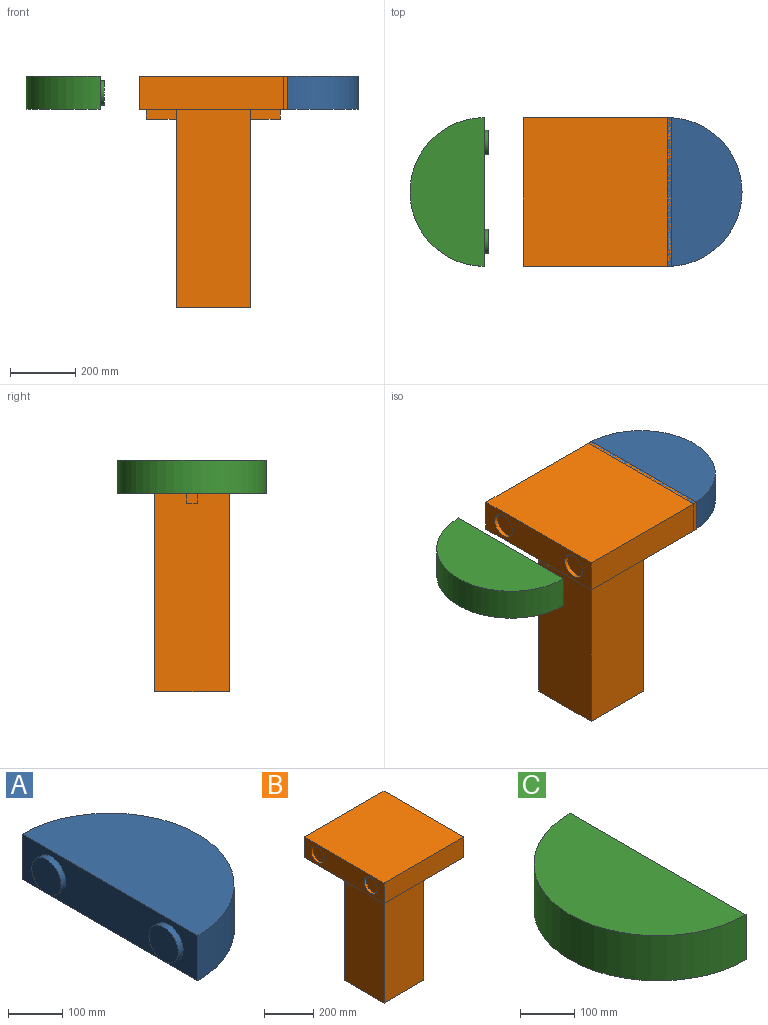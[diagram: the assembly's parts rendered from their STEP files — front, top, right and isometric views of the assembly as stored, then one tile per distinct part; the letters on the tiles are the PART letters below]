
ASSEMBLY  parts=3 mates=2
PART A: 8 faces, bbox 241.4x457.2x101.6 mm
  f0: plane 457.2x101.6mm, normal (-1,0,0), area 37330.8mm2, adj f1,f2,f3,f4,f6
  f1: cylinder r=228.6mm len=457.2mm, axis (0,0,-1), area 72965.9mm2, adj f0,f2,f3
  f2: plane 457.2x228.6mm, normal (0,0,1), area 82086.6mm2, adj f0,f1
  f3: plane 457.2x228.6mm, normal (0,0,-1), area 82086.6mm2, adj f0,f1
  f4: cylinder r=38.1mm len=76.2mm, axis (1,0,0), area 3064.6mm2, adj f0,f5
  f5: plane 76.2x76.2mm, normal (-1,0,0), area 4560.4mm2, adj f4
  f6: cylinder r=38.1mm len=76.2mm, axis (1,0,0), area 3064.6mm2, adj f0,f7
  f7: plane 76.2x76.2mm, normal (-1,0,0), area 4560.4mm2, adj f6
PART B: 27 faces, bbox 457.2x457.2x711.2 mm
  f0: plane 457.2x457.2mm, normal (0,0,-1), area 150642.3mm2, adj f1,f2,f3,f4,f14,f15,f16,f17
  f1: plane 457.2x101.6mm, normal (0,-1,0), area 46451.5mm2, adj f0,f2,f4,f5
  f2: plane 457.2x101.6mm, normal (1,0,0), area 37330.8mm2, adj f0,f1,f3,f5,f10,f12
  f3: plane 457.2x101.6mm, normal (0,1,0), area 46451.5mm2, adj f0,f2,f4,f5
  f4: plane 457.2x101.6mm, normal (-1,0,0), area 37330.8mm2, adj f0,f1,f3,f5,f6,f8
  f5: plane 457.2x457.2mm, normal (0,0,1), area 209031.8mm2, adj f1,f2,f3,f4
  f6: cylinder r=38.1mm len=76.2mm, axis (-1,0,0), area 3064.6mm2, adj f4,f7
  f7: plane 76.2x76.2mm, normal (-1,0,0), area 4560.4mm2, adj f6
  f8: cylinder r=38.1mm len=76.2mm, axis (-1,0,0), area 3064.6mm2, adj f4,f9
  f9: plane 76.2x76.2mm, normal (-1,0,0), area 4560.4mm2, adj f8
  f10: cylinder r=38.1mm len=76.2mm, axis (1,0,0), area 3064.6mm2, adj f2,f11
  f11: plane 76.2x76.2mm, normal (1,0,0), area 4560.4mm2, adj f10
  f12: cylinder r=38.1mm len=76.2mm, axis (1,0,0), area 3064.6mm2, adj f2,f13
  f13: plane 76.2x76.2mm, normal (1,0,0), area 4560.4mm2, adj f12
  f14: plane 609.6x228.6mm, normal (1,0,0), area 138332.6mm2, adj f0,f15,f17,f18,f23,f24,f25
  f15: plane 609.6x228.6mm, normal (0,-1,0), area 139354.6mm2, adj f0,f14,f16,f18
  f16: plane 609.6x228.6mm, normal (-1,0,0), area 138332.6mm2, adj f0,f15,f17,f18,f19,f21,f22
  f17: plane 609.6x228.6mm, normal (0,1,0), area 139354.6mm2, adj f0,f14,f16,f18
  f18: plane 228.6x228.6mm, normal (0,0,-1), area 52258mm2, adj f14,f15,f16,f17
  f19: plane 91.44x33.53mm, normal (0,0,-1), area 3065.8mm2, adj f16,f20,f21,f22
  f20: plane 33.53x30.48mm, normal (-1,0,0), area 1021.9mm2, adj f0,f19,f21,f22
  f21: plane 91.44x30.48mm, normal (0,1,0), area 2787.1mm2, adj f0,f16,f19,f20
  f22: plane 91.44x30.48mm, normal (0,-1,0), area 2787.1mm2, adj f0,f16,f19,f20
  f23: plane 91.44x33.53mm, normal (0,0,-1), area 3065.8mm2, adj f14,f24,f25,f26
  f24: plane 91.44x30.48mm, normal (0,-1,0), area 2787.1mm2, adj f0,f14,f23,f26
  f25: plane 91.44x30.48mm, normal (0,1,0), area 2787.1mm2, adj f0,f14,f23,f26
  f26: plane 33.53x30.48mm, normal (1,0,0), area 1021.9mm2, adj f0,f23,f24,f25
PART C: 8 faces, bbox 241.3x457.2x101.6 mm
  f0: plane 457.2x101.6mm, normal (1,0,0), area 37330.8mm2, adj f1,f2,f3,f4,f6
  f1: cylinder r=228.6mm len=457.2mm, axis (0,0,-1), area 72965.9mm2, adj f0,f2,f3
  f2: plane 457.2x228.6mm, normal (0,0,1), area 82086.6mm2, adj f0,f1
  f3: plane 457.2x228.6mm, normal (0,0,-1), area 82086.6mm2, adj f0,f1
  f4: cylinder r=38.1mm len=76.2mm, axis (-1,0,0), area 3040.2mm2, adj f0,f5
  f5: plane 76.2x76.2mm, normal (1,0,0), area 4560.4mm2, adj f4
  f6: cylinder r=38.1mm len=76.2mm, axis (-1,0,0), area 3040.2mm2, adj f0,f7
  f7: plane 76.2x76.2mm, normal (1,0,0), area 4560.4mm2, adj f6
PLACE A t=(-56.62,-131.5,-404.46)mm
PLACE B t=(-272.83,-131.5,-404.46)mm
PLACE C t=(-620.46,-131.5,-404.46)mm
MATE slider B.f10 <-> A.f4  axis (1,0,0) through (-57.03,20.9,-353.66)mm
MATE slider C.f6 <-> B.f8  axis (1,0,0) through (-620.46,20.9,-353.66)mm
